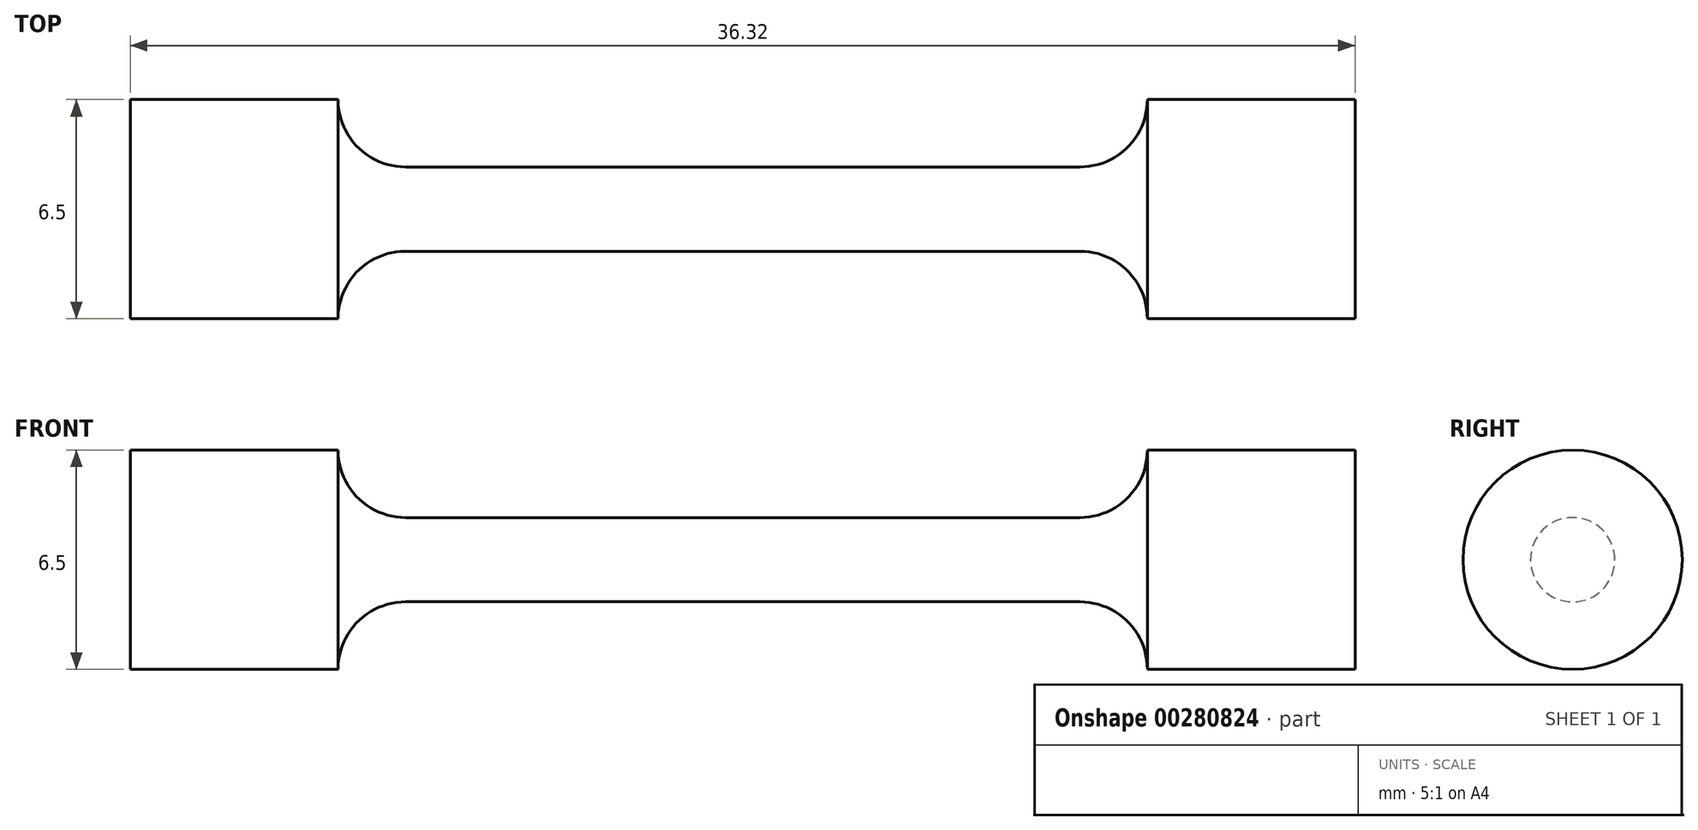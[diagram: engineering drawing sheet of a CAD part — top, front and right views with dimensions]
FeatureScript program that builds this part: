
annotation { "Feature Type Name" : "Feature", "Feature Type Description" : "" }
export const myFeature = defineFeature(function(context is Context, id is Id, definition is map)
    precondition{}
    {
        {
            var Q0;
            Q0=qCreatedBy(makeId("Front.planeOp"),FACE);
            var sketch = newSketch(context, id + "F0", { "sketchPlane" : qUnion([Q0])});
            skLineSegment(sketch, "E0", {"start": v(0, 1.25) * mm, "end": v(10, 1.25) * mm});
            skArc(sketch, "E1", {"start": v(10, 1.25) * mm, "mid": v(11.41, 1.84) * mm, "end": v(12, 3.25) * mm});
            skLineSegment(sketch, "E2", {"start": v(12, 3.25) * mm, "end": v(18.16, 3.25) * mm});
            skLineSegment(sketch, "E3", {"start": v(18.16, 3.25) * mm, "end": v(18.16, 0) * mm});
            skLineSegment(sketch, "E4.MirrorCS", {"start": v(0, 1.25) * mm, "end": v(-10, 1.25) * mm});
            skLineSegment(sketch, "E5.MirrorCS", {"start": v(-18.16, 3.25) * mm, "end": v(-18.16, 0) * mm});
            skLineSegment(sketch, "E6.MirrorCS", {"start": v(-12, 3.25) * mm, "end": v(-18.16, 3.25) * mm});
            skArc(sketch, "E7.MirrorCS", {"start": v(-10, 1.25) * mm, "mid": v(-11.41, 1.84) * mm, "end": v(-12, 3.25) * mm});
            skLineSegment(sketch, "E8", {"start": v(-18.16, 0) * mm, "end": v(18.16, 0) * mm});
            skSolve(sketch);
        }
        {
            var Q0;
            Q0 = qSketchRegion(id + "F0", true);
            var Q1;
            Q1=sQuery(id+"F0.wireOp",EDGE,"E8");
            revolve(context, id + "F1", {"entities" : qUnion([Q0]), "axis" : qUnion([Q1]), "revolveType" : RevolveType.FULL});
        }
    });
